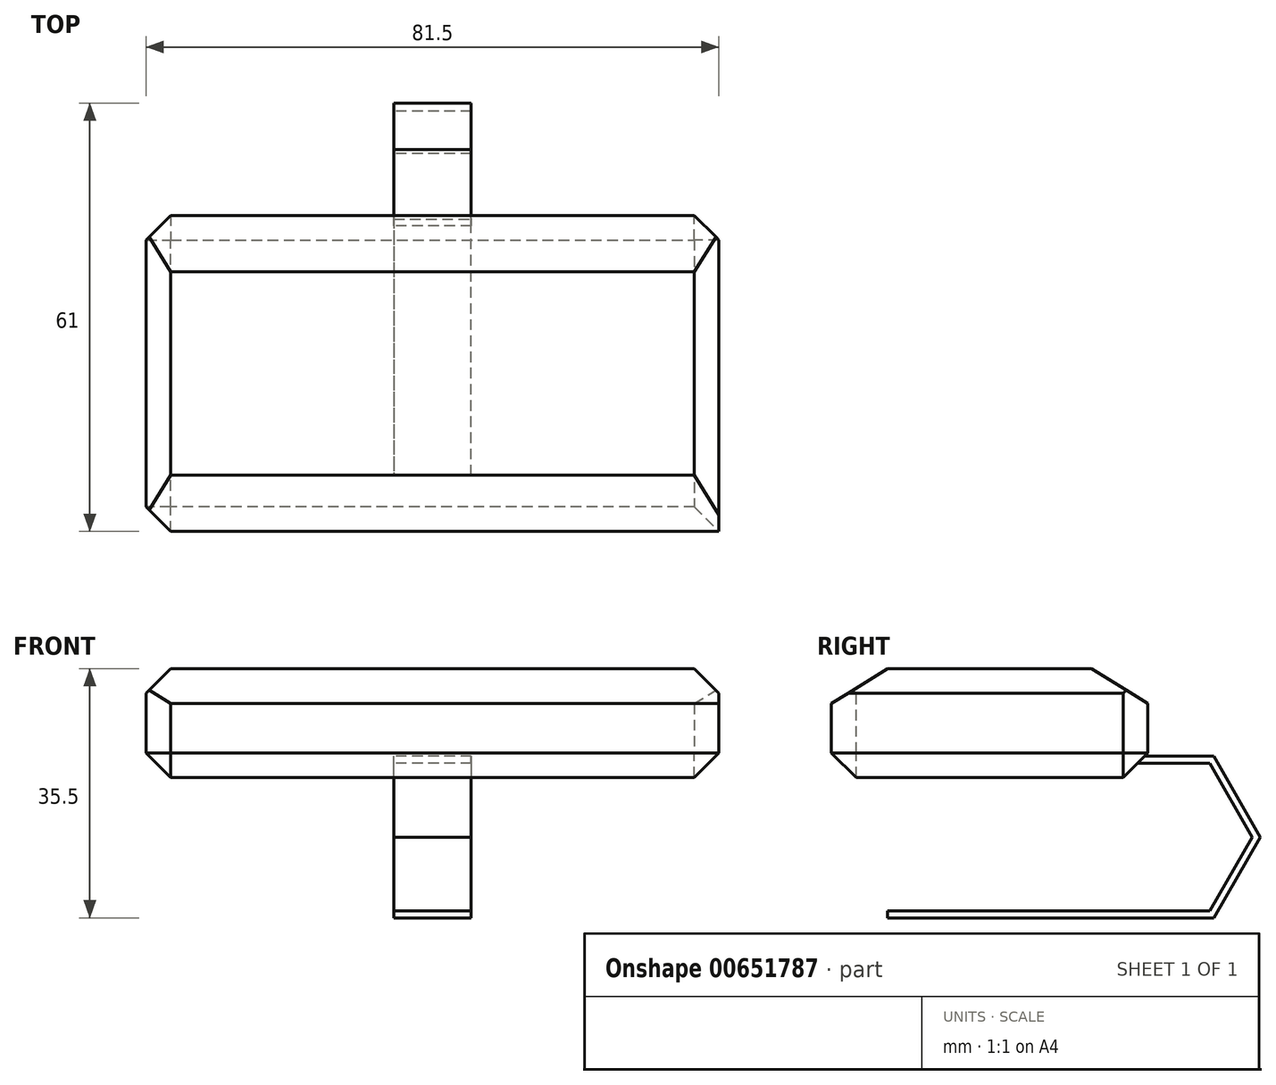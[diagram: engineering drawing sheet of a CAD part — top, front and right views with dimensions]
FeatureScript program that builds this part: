
annotation { "Feature Type Name" : "Feature", "Feature Type Description" : "" }
export const myFeature = defineFeature(function(context is Context, id is Id, definition is map)
    precondition{}
    {
        {
            var Q0;
            Q0=qCreatedBy(makeId("Top.planeOp"),FACE);
            var sketch = newSketch(context, id + "F0", { "sketchPlane" : qUnion([Q0])});
            skLineSegment(sketch, "E0.bottom", {"start": v(-26.01, 24.5) * mm, "end": v(55.49, 24.5) * mm});
            skLineSegment(sketch, "E0.top", {"start": v(-26.01, -20.5) * mm, "end": v(55.49, -20.5) * mm});
            skLineSegment(sketch, "E0.left", {"start": v(-26.01, 24.5) * mm, "end": v(-26.01, -20.5) * mm});
            skLineSegment(sketch, "E0.right", {"start": v(55.49, 24.5) * mm, "end": v(55.49, -20.5) * mm});
            skLineSegment(sketch, "E1", {"start": v(14.74, 24.5) * mm, "end": v(14.74, -32.57) * mm, "construction": true});
            skLineSegment(sketch, "E2", {"start": v(14.74, 24.5) * mm, "end": v(14.74, 62.12) * mm, "construction": true});
            skLineSegment(sketch, "E3", {"start": v(20.24, 24.5) * mm, "end": v(20.24, 40.5) * mm});
            skLineSegment(sketch, "E4", {"start": v(20.24, 40.5) * mm, "end": v(9.24, 40.5) * mm});
            skLineSegment(sketch, "E5", {"start": v(9.24, 40.5) * mm, "end": v(9.24, 24.5) * mm});
            skSolve(sketch);
        }
        {
            var Q0;
            Q0=makeQuery(id+"F0.imprint","IMPRINT",FACE,{"disambiguationData":[TD([[makeQuery(id+"F0.imprint","IMPRINT",EDGE,{"derivedFrom":sQuery(id+"F0.wireOp",EDGE,"E0.top")}),1.0]])]});
            extrude(context, id + "F1", {"entities" : qUnion([Q0]), "depth" : 15.5 * mm, "offsetDistance" : 25 * mm});
        }
        {
            var Q0;
            {var subQ0=sQuery(id+"F0.wireOp",EDGE,"E3");Q0=makeQuery(id+"F0.imprint","IMPRINT",FACE,{"disambiguationData":[TD([[makeQuery(id+"F0.imprint","IMPRINT",EDGE,{"derivedFrom":subQ0}),1.0]])]});}
            extrude(context, id + "F2", {"entities" : qUnion([Q0]), "operationType" : NewBodyOperationType.ADD, "oppositeDirection" : true, "depth" : 20 * mm, "offsetDistance" : 25 * mm, "hasSecondDirection" : true, "secondDirectionOppositeDirection" : false, "secondDirectionDepth" : 3 * mm});
        }
        {
            var Q0;
            Q0=makeQuery(id+"F2.opExtrude","SWEPT_FACE",FACE,{"disambiguationData":[OSD([sQuery(id+"F0.wireOp",EDGE,"E0.bottom")])]});
            extrude(context, id + "F3", {"entities" : qUnion([Q0]), "operationType" : NewBodyOperationType.ADD, "depth" : 37 * mm, "offsetDistance" : 25 * mm});
        }
        {
            var Q0;
            {var subQ0=sQuery(id+"F0.wireOp",EDGE,"E5");Q0=makeQuery(id+"F3.boolean.opBoolean","MERGE",FACE,{"derivedFrom":[makeQuery(id+"F2.opExtrude","SWEPT_FACE",FACE,{"disambiguationData":[OSD([subQ0])]}),makeQuery(id+"F3.opExtrude","SWEPT_FACE",FACE,{"disambiguationData":[OSD([sQuery(id+"F0.wireOp",EDGE,"E0.bottom"),subQ0])]})]});}
            var sketch = newSketch(context, id + "F4", { "sketchPlane" : qUnion([Q0])});
            skLineSegment(sketch, "E6", {"start": v(-40.5, -8.5) * mm, "end": v(12.5, -8.5) * mm, "construction": true});
            skLineSegment(sketch, "E7", {"start": v(-40.5, -8.5) * mm, "end": v(-33.9, 3) * mm});
            skLineSegment(sketch, "E8", {"start": v(-40.5, -8.5) * mm, "end": v(-33.9, -20) * mm});
            skSolve(sketch);
        }
        {
            var Q0;
            {var subQ0=sQuery(id+"F4.wireOp",EDGE,"E8");Q0=makeQuery(id+"F4.imprint","IMPRINT",FACE,{"disambiguationData":[TD([[makeQuery(id+"F4.imprint","IMPRINT",EDGE,{"derivedFrom":subQ0}),-1.0]])]});}
            var Q1;
            {var subQ0=sQuery(id+"F4.wireOp",EDGE,"E7");Q1=makeQuery(id+"F4.imprint","IMPRINT",FACE,{"disambiguationData":[TD([[makeQuery(id+"F4.imprint","IMPRINT",EDGE,{"derivedFrom":subQ0}),1.0]])]});}
            extrude(context, id + "F5", {"entities" : qUnion([Q0, Q1]), "operationType" : NewBodyOperationType.REMOVE, "oppositeDirection" : true, "depth" : 25 * mm, "offsetDistance" : 25 * mm});
        }
        {
            var Q0;
            {var subQ0=sQuery(id+"F0.wireOp",EDGE,"E5");Q0=makeQuery(id+"F3.boolean.opBoolean","MERGE",FACE,{"derivedFrom":[makeQuery(id+"F2.opExtrude","SWEPT_FACE",FACE,{"disambiguationData":[OSD([subQ0])]}),makeQuery(id+"F3.opExtrude","SWEPT_FACE",FACE,{"disambiguationData":[OSD([sQuery(id+"F0.wireOp",EDGE,"E0.bottom"),subQ0])]})]});}
            var sketch = newSketch(context, id + "F6", { "sketchPlane" : qUnion([Q0])});
            skLineSegment(sketch, "E9.0", {"start": v(-24.5, 0) * mm, "end": v(32.57, 0) * mm, "construction": true});
            skLineSegment(sketch, "E10", {"start": v(-34.46, 0) * mm, "end": v(-39.34, -8.5) * mm});
            skLineSegment(sketch, "E11", {"start": v(-39.34, -8.5) * mm, "end": v(-33.31, -19) * mm});
            skLineSegment(sketch, "E12", {"start": v(-33.31, -19) * mm, "end": v(12.5, -19) * mm});
            skLineSegment(sketch, "E13.0", {"start": v(12.5, -20) * mm, "end": v(-33.9, -20) * mm});
            skLineSegment(sketch, "E14.0", {"start": v(-40.5, -8.5) * mm, "end": v(-33.9, -20) * mm});
            skLineSegment(sketch, "E15.0", {"start": v(-40.5, -8.5) * mm, "end": v(-33.9, 3) * mm});
            skLineSegment(sketch, "E16", {"start": v(-24.5, 0) * mm, "end": v(12.5, 0) * mm});
            skLineSegment(sketch, "E17", {"start": v(12.5, 0) * mm, "end": v(-24.5, 0) * mm});
            skLineSegment(sketch, "E18.0", {"start": v(-24.5, 0) * mm, "end": v(-24.5, 3) * mm});
            skLineSegment(sketch, "E19", {"start": v(-24.5, 2) * mm, "end": v(-33.31, 2) * mm});
            skLineSegment(sketch, "E20", {"start": v(-34.46, 0) * mm, "end": v(-33.31, 2) * mm});
            skSolve(sketch);
        }
        {
            var Q0;
            {var subQ7=sQuery(id+"F6.wireOp",EDGE,"E10");Q0=makeQuery(id+"F6.imprint","IMPRINT",FACE,{"disambiguationData":[TD([[makeQuery(id+"F6.imprint","IMPRINT",EDGE,{"derivedFrom":subQ7}),1.0]])]});}
            extrude(context, id + "F7", {"entities" : qUnion([Q0]), "operationType" : NewBodyOperationType.REMOVE, "oppositeDirection" : true, "depth" : 25 * mm, "offsetDistance" : 25 * mm});
        }
        {
            var Q0;
            Q0=makeQuery(id+"F1.opExtrude","SWEPT_EDGE",EDGE,{"disambiguationData":[OSD([sQuery(id+"F0.wireOp",EDGE,"E0.bottom"),sQuery(id+"F0.wireOp",EDGE,"E0.left")])]});
            var Q1;
            Q1=makeQuery(id+"F1.opExtrude","SWEPT_EDGE",EDGE,{"disambiguationData":[OSD([sQuery(id+"F0.wireOp",EDGE,"E0.top"),sQuery(id+"F0.wireOp",EDGE,"E0.left")])]});
            var Q2;
            Q2=makeQuery(id+"F1.opExtrude","SWEPT_EDGE",EDGE,{"disambiguationData":[OSD([sQuery(id+"F0.wireOp",EDGE,"E0.bottom"),sQuery(id+"F0.wireOp",EDGE,"E0.right")])]});
            var Q3;
            Q3=makeQuery(id+"F1.opExtrude","CAP_EDGE",EDGE,{"disambiguationData":[OSD([sQuery(id+"F0.wireOp",EDGE,"E0.top")])],"isStart":true});
            var Q4;
            {var subQ0=sQuery(id+"F0.wireOp",EDGE,"E0.bottom");var subQ2=sQuery(id+"F0.wireOp",EDGE,"E0.right");var subQ3=sQuery(id+"F0.wireOp",EDGE,"E0.left");var subQ4=makeQuery(id+"F1.opExtrude","CAP_FACE",FACE,{"disambiguationData":[OSD([subQ0,sQuery(id+"F0.wireOp",EDGE,"E0.top"),subQ3,subQ2])],"isStart":true});var subQ5=makeQuery(id+"F1.opExtrude","SWEPT_FACE",FACE,{"disambiguationData":[OSD([subQ0])]});var subQ6=makeQuery(id+"F1.opExtrude","CAP_EDGE",EDGE,{"disambiguationData":[OSD([subQ0])],"isStart":true});Q4=makeQuery(id+"F7.boolean.opBoolean","MERGE",EDGE,{"derivedFrom":[makeQuery(id+"F2.boolean.opBoolean","SPLIT",EDGE,{"disambiguationData":[topologyDisambiguationEdgeConnected([subQ5,subQ4]),TD([makeQuery(id+"F1.opExtrude","SWEPT_FACE",FACE,{"disambiguationData":[OSD([subQ3])]})])],"derivedFrom":subQ6}),makeQuery(id+"F2.boolean.opBoolean","SPLIT",EDGE,{"disambiguationData":[topologyDisambiguationEdgeConnected([subQ5,subQ4]),TD([makeQuery(id+"F1.opExtrude","SWEPT_FACE",FACE,{"disambiguationData":[OSD([subQ2])]})])],"derivedFrom":subQ6}),makeQuery(id+"F7.opExtrude","SWEPT_EDGE",EDGE,{"disambiguationData":[OSD([sQuery(id+"F6.wireOp",EDGE,"E17"),sQuery(id+"F6.wireOp",EDGE,"E18.0")])]})]});}
            var Q5;
            Q5=makeQuery(id+"F1.opExtrude","CAP_EDGE",EDGE,{"disambiguationData":[OSD([sQuery(id+"F0.wireOp",EDGE,"E0.right")])],"isStart":true});
            var Q6;
            Q6=makeQuery(id+"F1.opExtrude","CAP_EDGE",EDGE,{"disambiguationData":[OSD([sQuery(id+"F0.wireOp",EDGE,"E0.left")])],"isStart":true});
            var Q7;
            Q7=makeQuery(id+"F1.opExtrude","CAP_EDGE",EDGE,{"disambiguationData":[OSD([sQuery(id+"F0.wireOp",EDGE,"E0.left")])],"isStart":false});
            var Q8;
            Q8=makeQuery(id+"F1.opExtrude","CAP_EDGE",EDGE,{"disambiguationData":[OSD([sQuery(id+"F0.wireOp",EDGE,"E0.right")])],"isStart":false});
            chamfer(context, id + "F8", {"entities" : qUnion([Q0, Q1, Q2, Q3, Q4, Q5, Q6, Q7, Q8]), "width" : 3.5 * mm, "tangentPropagation" : true});
        }
        {
            var Q0;
            Q0=makeQuery(id+"F1.opExtrude","CAP_EDGE",EDGE,{"disambiguationData":[OSD([sQuery(id+"F0.wireOp",EDGE,"E0.bottom")])],"isStart":false});
            var Q1;
            Q1=makeQuery(id+"F1.opExtrude","CAP_EDGE",EDGE,{"disambiguationData":[OSD([sQuery(id+"F0.wireOp",EDGE,"E0.top")])],"isStart":false});
            chamfer(context, id + "F9", {"entities" : qUnion([Q0, Q1]), "chamferType" : ChamferType.TWO_OFFSETS, "width1" : 5 * mm, "oppositeDirection" : false, "width2" : 8 * mm, "tangentPropagation" : true});
        }
    });
